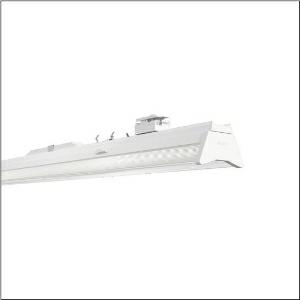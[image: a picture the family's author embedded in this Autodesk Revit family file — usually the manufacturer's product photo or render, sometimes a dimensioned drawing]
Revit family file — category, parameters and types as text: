
# Revit family: licross_21_performance_mo_51td16vn465g
name_source: partatom
category: Lighting Fixtures
units: mm (PartAtom-declared; Revit-internal decimal feet)

## family parameters
Cut with Voids When Loaded = No
Host = Face
Light Source = No
Part Type = Normal
Room Calculation Point = No
Round Connector Dimension = Use Diameter
Shared = No

## types (1)
- --- (1 x LED, 6500 lm, 34.9 W, 4000K)
    Apparent Load = 35 VA
    CIE Flux Codes = 66 88 96 79 100
    Color Rendering = 80
    Color Temperature = 4000K
    Default Elevation = 1800 mm
    Description = Licross 21 Performance MO, luminaire insert, of sheet steel, galvanised, coil coated, white, length: 1.500mm, width: 120mm, height: 123mm, LED rated luminous flux: 6.500lm, light colour: 840, SDCM (Standard Deviation of Colour Matching)MacAdam ≤ 2 SDCM (initial), control gear: DALI 2, CLO, with plug, 5-pole, with phase selection, mains connection: 220..240V, AC, 50/60Hz, start of lifetime: 35W, end of service life: 38W, internal wiring halogen-free, primary light control with lens, of plastic, primary optical cover: cover, of PMMA, light emission: direct/indirect distribution, primary light characteristic: symmetric, protection rating (complete): IP54, insulation class (complete): insulation class I (protective earthing), certification: CE, ENEC, VDE, UKCA, protection symbol: D if used in an environment with non-conductive dust loads with corresponding accessories, impact resistance: IK06, permissible ambient temperature for indoor applications: -25..+40°C, corresponds to IFS (International Featured Standards) requirements for safety and quality in the food industry, reducing of maximum allowable ambient temperature of 5°C with ceiling mounting, LABS conformity tested according to VDMA 24364:2018-05, The light source and the operating device comply with the requirements of the Ecodesign Regulation (EU) 2019/2020 and are replaceable in accordance with this regulation, packaging unit: 1 piece
    Height = 114 mm
    Lamp = 1 x LED
    Lamp Light Flux = 6500 lm
    Lamp Power = 34.9 W
    Lamp count = 1
    Length = 1500 mm
    Luminous efficacy = 186 lm/W
    Manufacturer = Siteco
    ModVariant = No
    Model = 51TD16VN465G
    Mounting Place = Ceiling
    Mounting Type = Pendant
    Number of Poles = 1
    OnlyDefault = Yes
    Power Factor = 1
    Product Name = Licross 21 Performance MO
    Product group = luminaire insert | ceiling pendant
    ProductGroupID = 901
    Protection Class = Protection class I
    Protection Degree = IP 54
    RLX_Detail_Level = 1
    RLX_Emergency_Light_Flux = 0 lm
    RLX_Emergency_Type = 0
    RLX_Emergency_Type_DB = No
    RlxData = <blob elided: 34313 chars, md5=8c2e6e43>
    Socket = socket
    Standby Power = 0 W
    System Light Flux = 6500 lm
    System Power = 35 W
    Type Comments = factory setting: luminous flux: 100 % | dim-lin: 254 | 236 mA
    Type Image = l_1256138.jpg
    URL = http://relux.com
    VarID = @adj_093203
    Voltage = 0 V
    Weight = 0.00 kg
    Width = 120 mm

## geometry (parser evidence)
native form markers: Blend x4, Sweep x14
no freeform markers — native parametric forms only
